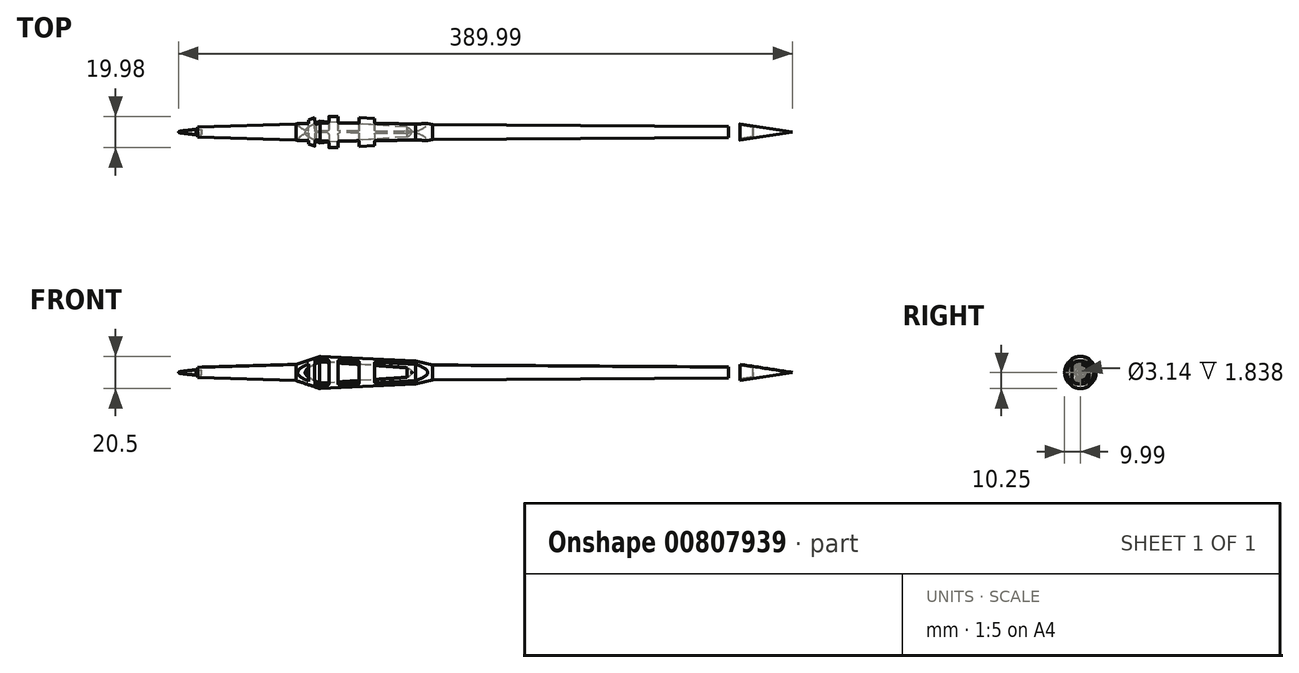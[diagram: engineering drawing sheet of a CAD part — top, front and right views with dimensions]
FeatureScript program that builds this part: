
annotation { "Feature Type Name" : "Feature", "Feature Type Description" : "" }
export const myFeature = defineFeature(function(context is Context, id is Id, definition is map)
    precondition{}
    {
        {
            var Q0;
            Q0=qCreatedBy(makeId("Right.planeOp"),FACE);
            var sketch = newSketch(context, id + "F0", { "sketchPlane" : qUnion([Q0])});
            skCircle(sketch, "E0", {"center": v(0, 0) * mm, "radius": 16.1 * mm});
            skSolve(sketch);
        }
        {
            var Q0;
            Q0=qCreatedBy(makeId("Front.planeOp"),FACE);
            var sketch = newSketch(context, id + "F1", { "sketchPlane" : qUnion([Q0])});
            skLineSegment(sketch, "E1", {"start": v(-173.44, 0) * mm, "end": v(-110.98, 0) * mm});
            skLineSegment(sketch, "E2", {"start": v(-110.98, 0) * mm, "end": v(-110.98, 5.13) * mm});
            skLineSegment(sketch, "E3", {"start": v(-110.98, 5.13) * mm, "end": v(-173.44, 3.3) * mm});
            skLineSegment(sketch, "E4", {"start": v(-173.44, 3.3) * mm, "end": v(-173.43, 2.8) * mm});
            skLineSegment(sketch, "E5", {"start": v(-173.43, 2.8) * mm, "end": v(-171.93, 0) * mm});
            skSolve(sketch);
        }
        {
            var Q0;
            Q0 = qSketchRegion(id + "F1", true);
            var Q1;
            Q1=sQuery(id+"F0.wireOp",EDGE,"E0");
            revolve(context, id + "F2", {"surfaceOperationType" : NewSurfaceOperationType.NEW, "entities" : qUnion([Q0]), "axis" : qUnion([Q1]), "revolveType" : RevolveType.FULL});
        }
        {
            var Q0;
            Q0=qCreatedBy(makeId("Front.planeOp"),FACE);
            var sketch = newSketch(context, id + "F3", { "sketchPlane" : qUnion([Q0])});
            skLineSegment(sketch, "E6.0", {"start": v(-110.98, -5.13) * mm, "end": v(-110.98, 5.13) * mm});
            skLineSegment(sketch, "E7", {"start": v(-110.98, 5.13) * mm, "end": v(-95.6, 10.25) * mm});
            skLineSegment(sketch, "E8", {"start": v(-95.6, 10.25) * mm, "end": v(-35.2, 7.33) * mm});
            skLineSegment(sketch, "E9", {"start": v(-35.2, 7.33) * mm, "end": v(-24.39, 4.74) * mm});
            skLineSegment(sketch, "E10", {"start": v(-24.39, 4.74) * mm, "end": v(-24.39, 0) * mm});
            skLineSegment(sketch, "E11", {"start": v(-24.39, 0) * mm, "end": v(-110.98, 0) * mm});
            skSolve(sketch);
        }
        {
            var Q0;
            Q0 = qSketchRegion(id + "F3", true);
            var Q1;
            Q1=makeQuery(id+"F2.opRevolve","SWEPT_EDGE",EDGE,{"disambiguationData":[OSD([sQuery(id+"F1.wireOp",EDGE,"E2"),sQuery(id+"F1.wireOp",EDGE,"E3")])]});
            revolve(context, id + "F4", {"surfaceOperationType" : NewSurfaceOperationType.NEW, "entities" : qUnion([Q0]), "axis" : qUnion([Q1]), "revolveType" : RevolveType.FULL});
        }
        {
            var Q0;
            Q0=qCreatedBy(makeId("Front.planeOp"),FACE);
            var sketch = newSketch(context, id + "F5", { "sketchPlane" : qUnion([Q0])});
            skLineSegment(sketch, "E12.0", {"start": v(-24.39, 4.74) * mm, "end": v(-24.39, -4.74) * mm});
            skLineSegment(sketch, "E13", {"start": v(-24.39, 4.74) * mm, "end": v(163.57, 3.5) * mm});
            skLineSegment(sketch, "E14", {"start": v(163.57, 3.5) * mm, "end": v(163.57, 0) * mm});
            skLineSegment(sketch, "E15", {"start": v(163.57, 0) * mm, "end": v(-24.39, 0) * mm});
            skSolve(sketch);
        }
        {
            var Q0;
            Q0 = qSketchRegion(id + "F5", true);
            var Q1;
            Q1=makeQuery(id+"F4.opRevolve","SWEPT_EDGE",EDGE,{"disambiguationData":[OSD([sQuery(id+"F3.wireOp",EDGE,"E9"),sQuery(id+"F3.wireOp",EDGE,"E10")])]});
            revolve(context, id + "F6", {"operationType" : NewBodyOperationType.ADD, "surfaceOperationType" : NewSurfaceOperationType.NEW, "entities" : qUnion([Q0]), "axis" : qUnion([Q1]), "revolveType" : RevolveType.FULL});
        }
        {
            var Q0;
            Q0=qCreatedBy(makeId("Front.planeOp"),FACE);
            var sketch = newSketch(context, id + "F7", { "sketchPlane" : qUnion([Q0])});
            skLineSegment(sketch, "E16", {"start": v(170.8, -5.14) * mm, "end": v(204.34, 0) * mm});
            skLineSegment(sketch, "E17", {"start": v(204.34, 0) * mm, "end": v(179.09, 0) * mm});
            skPoint(sketch, "E18.orphan", {"position": v(170.8, 5.14) * mm});
            skLineSegment(sketch, "E19", {"start": v(170.8, -5.14) * mm, "end": v(170.8, -4.26) * mm});
            skLineSegment(sketch, "E20", {"start": v(170.8, -4.26) * mm, "end": v(179.09, -3) * mm});
            skLineSegment(sketch, "E21", {"start": v(179.09, -3) * mm, "end": v(179.09, 0) * mm});
            skPoint(sketch, "E22.orphan", {"position": v(170.8, 0) * mm});
            skSolve(sketch);
        }
        {
            var Q0;
            Q0 = qSketchRegion(id + "F7", true);
            var Q1;
            Q1=sQuery(id+"F7.wireOp",EDGE,"E17");
            revolve(context, id + "F8", {"surfaceOperationType" : NewSurfaceOperationType.NEW, "entities" : qUnion([Q0]), "axis" : qUnion([Q1]), "revolveType" : RevolveType.FULL});
        }
        {
            var Q0;
            Q0=qCreatedBy(makeId("Front.planeOp"),FACE);
            var sketch = newSketch(context, id + "F9", { "sketchPlane" : qUnion([Q0])});
            skLineSegment(sketch, "E23", {"start": v(-105.41, 0) * mm, "end": v(-37.44, 0) * mm});
            skLineSegment(sketch, "E24", {"start": v(-96.12, 6.85) * mm, "end": v(-40.55, 3.12) * mm});
            skFitSpline(sketch, "E25", {"points": [v(-40.55, 3.12) * mm, v(-39.27, 2.42) * mm, v(-38.02, 1.33) * mm, v(-37.56, 0.61) * mm, v(-37.44, 0) * mm], "startDerivative": vector(4.44, -2.14) * mm, "endDerivative": vector(0.4, -3.29) * mm});
            skFitSpline(sketch, "E26", {"points": [v(-105.41, 0) * mm, v(-105.33, 0.62) * mm, v(-104.64, 1.81) * mm, v(-103.44, 2.78) * mm, v(-101.54, 3.98) * mm, v(-98.36, 5.7) * mm, v(-96.12, 6.85) * mm], "startDerivative": vector(0.12, 5.92) * mm, "endDerivative": vector(10.8, 5.6) * mm});
            skSolve(sketch);
        }
        {
            var Q0;
            Q0 = qSketchRegion(id + "F9", true);
            var Q1;
            Q1=sQuery(id+"F9.wireOp",EDGE,"E23");
            revolve(context, id + "F10", {"surfaceOperationType" : NewSurfaceOperationType.NEW, "entities" : qUnion([Q0]), "axis" : qUnion([Q1]), "revolveType" : RevolveType.FULL});
        }
        {
            var Q0;
            Q0=qCreatedBy(makeId("Front.planeOp"),FACE);
            cPlane(context, id + "F11", {"entities" : qUnion([Q0]), "cplaneType" : CPlaneType.OFFSET, "offset" : 5.5 * mm, "width" : 150 * mm, "height" : 150 * mm});
        }
        {
            var Q0;
            Q0=qCreatedBy(id+"F11.planeOp",FACE);
            var sketch = newSketch(context, id + "F12", { "sketchPlane" : qUnion([Q0])});
            skLineSegment(sketch, "E27", {"start": v(-103.15, 5.55) * mm, "end": v(-103.15, 0) * mm});
            skLineSegment(sketch, "E28", {"start": v(-103.15, 0) * mm, "end": v(-109.96, 0) * mm});
            skFitSpline(sketch, "E29", {"points": [v(-109.96, 0) * mm, v(-109.82, 0.74) * mm, v(-109.26, 1.7) * mm, v(-107.77, 3.02) * mm, v(-103.15, 5.55) * mm], "startDerivative": vector(0.52, 4.74) * mm, "endDerivative": vector(12.88, 6.48) * mm});
            skPoint(sketch, "E30.orphan", {"position": v(-72.07, 0) * mm});
            skLineSegment(sketch, "E31", {"start": v(-99.33, 0) * mm, "end": v(-90.18, 0) * mm});
            skLineSegment(sketch, "E32", {"start": v(-99.33, 0) * mm, "end": v(-99.05, 6.84) * mm});
            skLineSegment(sketch, "E33", {"start": v(-98.28, 7.82) * mm, "end": v(-96.53, 8.42) * mm});
            skLineSegment(sketch, "E34", {"start": v(-90.18, 0) * mm, "end": v(-90.18, 7.22) * mm});
            skLineSegment(sketch, "E35", {"start": v(-84.46, 0) * mm, "end": v(-84.46, 6.81) * mm});
            skLineSegment(sketch, "E36", {"start": v(-96.15, 8.48) * mm, "end": v(-91.13, 8.22) * mm});
            skLineSegment(sketch, "E37", {"start": v(-70.96, 0) * mm, "end": v(-70.96, 6.78) * mm});
            skLineSegment(sketch, "E38", {"start": v(-61.15, 0) * mm, "end": v(-61.15, 5.96) * mm});
            skFitSpline(sketch, "E39", {"points": [v(-35.21, 5.3) * mm, v(-33, 4.43) * mm, v(-30.49, 3.26) * mm, v(-28.4, 1.84) * mm, v(-27.66, 0.93) * mm, v(-27.4, 0) * mm], "startDerivative": vector(9.73, -3.74) * mm, "endDerivative": vector(1.3, -6.7) * mm});
            skArc(sketch, "E40", {"start": v(-60.47, 6.62) * mm, "mid": v(-60.95, 6.44) * mm, "end": v(-61.15, 5.96) * mm});
            skArc(sketch, "E41", {"start": v(-70.96, 6.78) * mm, "mid": v(-71.05, 7.04) * mm, "end": v(-71.28, 7.18) * mm});
            skArc(sketch, "E42.filletArc", {"start": v(-83.4, 7.81) * mm, "mid": v(-84.15, 7.54) * mm, "end": v(-84.46, 6.81) * mm});
            skArc(sketch, "E43.filletArc", {"start": v(-90.18, 7.22) * mm, "mid": v(-90.45, 7.9) * mm, "end": v(-91.13, 8.22) * mm});
            skFitSpline(sketch, "E44", {"points": [v(-99.05, 6.84) * mm, v(-98.95, 7.26) * mm, v(-98.7, 7.57) * mm, v(-98.28, 7.82) * mm], "startDerivative": vector(0.2, 1.33) * mm, "endDerivative": vector(1.27, 0.66) * mm});
            skLineSegment(sketch, "E45", {"start": v(-83.4, 7.81) * mm, "end": v(-71.28, 7.18) * mm});
            skLineSegment(sketch, "E46", {"start": v(-60.47, 6.62) * mm, "end": v(-35.21, 5.3) * mm});
            skLineSegment(sketch, "E47.trimOffspring", {"start": v(-61.15, 0) * mm, "end": v(-27.4, 0) * mm});
            skLineSegment(sketch, "E48.trimOffspring", {"start": v(-84.46, 0) * mm, "end": v(-70.96, 0) * mm});
            skPoint(sketch, "E49.visualSharp", {"position": v(-96.34, 8.49) * mm});
            skArc(sketch, "E49.filletArc", {"start": v(-96.15, 8.48) * mm, "mid": v(-96.34, 8.47) * mm, "end": v(-96.53, 8.42) * mm});
            skSolve(sketch);
        }
        {
            var Q0;
            Q0 = qSketchRegion(id + "F12", true);
            var Q1;
            Q1=sQuery(id+"F12.wireOp",EDGE,"E28");
            revolve(context, id + "F13", {"surfaceOperationType" : NewSurfaceOperationType.NEW, "entities" : qUnion([Q0]), "axis" : qUnion([Q1]), "revolveType" : RevolveType.FULL});
        }
        {
            var Q0;
            Q0=makeQuery(id+"F13.opRevolve","SWEPT_BODY",BODY,{"disambiguationData":[OSD([sQuery(id+"F12.wireOp",EDGE,"E27"),sQuery(id+"F12.wireOp",EDGE,"E28"),sQuery(id+"F12.wireOp",EDGE,"E29")])]});
            var Q1;
            Q1=makeQuery(id+"F13.opRevolve","SWEPT_BODY",BODY,{"disambiguationData":[OSD([sQuery(id+"F12.wireOp",EDGE,"E31"),sQuery(id+"F12.wireOp",EDGE,"E32"),sQuery(id+"F12.wireOp",EDGE,"E33"),sQuery(id+"F12.wireOp",EDGE,"E34"),sQuery(id+"F12.wireOp",EDGE,"E36"),sQuery(id+"F12.wireOp",EDGE,"E43.filletArc"),sQuery(id+"F12.wireOp",EDGE,"E44")])]});
            var Q2;
            Q2=makeQuery(id+"F13.opRevolve","SWEPT_BODY",BODY,{"disambiguationData":[OSD([sQuery(id+"F12.wireOp",EDGE,"E35"),sQuery(id+"F12.wireOp",EDGE,"E37"),sQuery(id+"F12.wireOp",EDGE,"E41"),sQuery(id+"F12.wireOp",EDGE,"E42.filletArc"),sQuery(id+"F12.wireOp",EDGE,"E45"),sQuery(id+"F12.wireOp",EDGE,"E48.trimOffspring")])]});
            var Q3;
            Q3=makeQuery(id+"F13.opRevolve","SWEPT_BODY",BODY,{"disambiguationData":[OSD([sQuery(id+"F12.wireOp",EDGE,"E38"),sQuery(id+"F12.wireOp",EDGE,"E39"),sQuery(id+"F12.wireOp",EDGE,"E40"),sQuery(id+"F12.wireOp",EDGE,"E46"),sQuery(id+"F12.wireOp",EDGE,"E47.trimOffspring")])]});
            var Q4;
            Q4=qCreatedBy(makeId("Front.planeOp"),FACE);
            mirror(context, id + "F14", {"entities" : qUnion([Q0, Q1, Q2, Q3]), "mirrorPlane" : qUnion([Q4])});
        }
        {
            var Q0;
            Q0=makeQuery(id+"F14.opPattern","COPY",BODY,{"derivedFrom":makeQuery(id+"F13.opRevolve","SWEPT_BODY",BODY,{"disambiguationData":[OSD([sQuery(id+"F12.wireOp",EDGE,"E27"),sQuery(id+"F12.wireOp",EDGE,"E28"),sQuery(id+"F12.wireOp",EDGE,"E29")])]}),"instanceName":"1"});
            var Q1;
            Q1=makeQuery(id+"F13.opRevolve","SWEPT_BODY",BODY,{"disambiguationData":[OSD([sQuery(id+"F12.wireOp",EDGE,"E27"),sQuery(id+"F12.wireOp",EDGE,"E28"),sQuery(id+"F12.wireOp",EDGE,"E29")])]});
            var Q2;
            Q2=makeQuery(id+"F13.opRevolve","SWEPT_BODY",BODY,{"disambiguationData":[OSD([sQuery(id+"F12.wireOp",EDGE,"E31"),sQuery(id+"F12.wireOp",EDGE,"E32"),sQuery(id+"F12.wireOp",EDGE,"E33"),sQuery(id+"F12.wireOp",EDGE,"E34"),sQuery(id+"F12.wireOp",EDGE,"E36"),sQuery(id+"F12.wireOp",EDGE,"E43.filletArc"),sQuery(id+"F12.wireOp",EDGE,"E44")])]});
            var Q3;
            Q3=makeQuery(id+"F13.opRevolve","SWEPT_BODY",BODY,{"disambiguationData":[OSD([sQuery(id+"F12.wireOp",EDGE,"E35"),sQuery(id+"F12.wireOp",EDGE,"E37"),sQuery(id+"F12.wireOp",EDGE,"E41"),sQuery(id+"F12.wireOp",EDGE,"E42.filletArc"),sQuery(id+"F12.wireOp",EDGE,"E45"),sQuery(id+"F12.wireOp",EDGE,"E48.trimOffspring")])]});
            var Q4;
            Q4=makeQuery(id+"F13.opRevolve","SWEPT_BODY",BODY,{"disambiguationData":[OSD([sQuery(id+"F12.wireOp",EDGE,"E38"),sQuery(id+"F12.wireOp",EDGE,"E39"),sQuery(id+"F12.wireOp",EDGE,"E40"),sQuery(id+"F12.wireOp",EDGE,"E46"),sQuery(id+"F12.wireOp",EDGE,"E47.trimOffspring")])]});
            var Q5;
            Q5=makeQuery(id+"F14.opPattern","COPY",BODY,{"derivedFrom":makeQuery(id+"F13.opRevolve","SWEPT_BODY",BODY,{"disambiguationData":[OSD([sQuery(id+"F12.wireOp",EDGE,"E38"),sQuery(id+"F12.wireOp",EDGE,"E39"),sQuery(id+"F12.wireOp",EDGE,"E40"),sQuery(id+"F12.wireOp",EDGE,"E46"),sQuery(id+"F12.wireOp",EDGE,"E47.trimOffspring")])]}),"instanceName":"1"});
            var Q6;
            Q6=makeQuery(id+"F14.opPattern","COPY",BODY,{"derivedFrom":makeQuery(id+"F13.opRevolve","SWEPT_BODY",BODY,{"disambiguationData":[OSD([sQuery(id+"F12.wireOp",EDGE,"E35"),sQuery(id+"F12.wireOp",EDGE,"E37"),sQuery(id+"F12.wireOp",EDGE,"E41"),sQuery(id+"F12.wireOp",EDGE,"E42.filletArc"),sQuery(id+"F12.wireOp",EDGE,"E45"),sQuery(id+"F12.wireOp",EDGE,"E48.trimOffspring")])]}),"instanceName":"1"});
            var Q7;
            Q7=makeQuery(id+"F14.opPattern","COPY",BODY,{"derivedFrom":makeQuery(id+"F13.opRevolve","SWEPT_BODY",BODY,{"disambiguationData":[OSD([sQuery(id+"F12.wireOp",EDGE,"E31"),sQuery(id+"F12.wireOp",EDGE,"E32"),sQuery(id+"F12.wireOp",EDGE,"E33"),sQuery(id+"F12.wireOp",EDGE,"E34"),sQuery(id+"F12.wireOp",EDGE,"E36"),sQuery(id+"F12.wireOp",EDGE,"E43.filletArc"),sQuery(id+"F12.wireOp",EDGE,"E44")])]}),"instanceName":"1"});
            var Q8;
            Q8=makeQuery(id+"F4.opRevolve","SWEPT_BODY",BODY,{"disambiguationData":[OSD([sQuery(id+"F3.wireOp",EDGE,"E6.0"),sQuery(id+"F3.wireOp",EDGE,"E7"),sQuery(id+"F3.wireOp",EDGE,"E8"),sQuery(id+"F3.wireOp",EDGE,"E9"),sQuery(id+"F3.wireOp",EDGE,"E10"),sQuery(id+"F3.wireOp",EDGE,"E11")])]});
            booleanBodies(context, id + "F15", {"operationType" : BooleanOperationType.SUBTRACTION, "tools" : qUnion([Q0, Q1, Q2, Q3, Q4, Q5, Q6, Q7]), "targets" : qUnion([Q8])});
        }
        {
            var Q0;
            Q0=qCreatedBy(makeId("Front.planeOp"),FACE);
            var sketch = newSketch(context, id + "F16", { "sketchPlane" : qUnion([Q0])});
            skLineSegment(sketch, "E50", {"start": v(0, 0) * mm, "end": v(-193.66, 0) * mm});
            skFitSpline(sketch, "E51", {"points": [v(-185.65, 0) * mm, v(-185.54, 0.27) * mm, v(-184.9, 0.47) * mm, v(-176.75, 1.45) * mm, v(-174.46, 1.57) * mm], "startDerivative": vector(0.87, 3.18) * mm, "endDerivative": vector(6.26, 0.09) * mm});
            skLineSegment(sketch, "E52", {"start": v(-174.46, 1.57) * mm, "end": v(-170.93, 1.57) * mm});
            skLineSegment(sketch, "E53", {"start": v(-170.93, 1.57) * mm, "end": v(-170.93, 0) * mm});
            skSolve(sketch);
        }
        {
            var Q0;
            Q0 = qSketchRegion(id + "F16", true);
            var Q1;
            Q1=sQuery(id+"F16.wireOp",EDGE,"E50");
            revolve(context, id + "F17", {"surfaceOperationType" : NewSurfaceOperationType.NEW, "entities" : qUnion([Q0]), "axis" : qUnion([Q1]), "revolveType" : RevolveType.FULL});
        }
        {
            var Q0;
            Q0=makeQuery(id+"F17.opRevolve","SWEPT_BODY",BODY,{"disambiguationData":[OSD([sQuery(id+"F16.wireOp",EDGE,"E50"),sQuery(id+"F16.wireOp",EDGE,"E51"),sQuery(id+"F16.wireOp",EDGE,"E52"),sQuery(id+"F16.wireOp",EDGE,"E53")])]});
            transform(context, id + "F18", {"entities" : qUnion([Q0]), "transformType" : TransformType.TRANSLATION_3D, "dx" : 0 * mm, "dy" : 0 * mm, "dz" : 0 * mm, "makeCopy" : true});
        }
        {
            var Q0;
            Q0=makeQuery(id+"F18.opPattern","COPY",BODY,{"derivedFrom":makeQuery(id+"F17.opRevolve","SWEPT_BODY",BODY,{"disambiguationData":[OSD([sQuery(id+"F16.wireOp",EDGE,"E50"),sQuery(id+"F16.wireOp",EDGE,"E51"),sQuery(id+"F16.wireOp",EDGE,"E52"),sQuery(id+"F16.wireOp",EDGE,"E53")])]}),"instanceName":"1"});
            var Q1;
            Q1=makeQuery(id+"F2.opRevolve","SWEPT_BODY",BODY,{"disambiguationData":[OSD([sQuery(id+"F1.wireOp",EDGE,"E1"),sQuery(id+"F1.wireOp",EDGE,"E2"),sQuery(id+"F1.wireOp",EDGE,"E3"),sQuery(id+"F1.wireOp",EDGE,"EPHL8iwW-0kiM-ldp9-sbAc-f7dRZdCR8gQH")])]});
            booleanBodies(context, id + "F19", {"operationType" : BooleanOperationType.SUBTRACTION, "tools" : qUnion([Q0]), "targets" : qUnion([Q1])});
        }
        {
            var Q0;
            Q0=makeQuery(id+"F10.opRevolve","SWEPT_BODY",BODY,{"disambiguationData":[OSD([sQuery(id+"F9.wireOp",EDGE,"E23"),sQuery(id+"F9.wireOp",EDGE,"E24"),sQuery(id+"F9.wireOp",EDGE,"E25"),sQuery(id+"F9.wireOp",EDGE,"E26")])]});
            transform(context, id + "F20", {"entities" : qUnion([Q0]), "transformType" : TransformType.TRANSLATION_3D, "dx" : 0 * mm, "dy" : 0 * mm, "dz" : 0 * mm, "makeCopy" : true});
        }
        {
            var Q0;
            Q0=makeQuery(id+"F20.opPattern","COPY",BODY,{"derivedFrom":makeQuery(id+"F10.opRevolve","SWEPT_BODY",BODY,{"disambiguationData":[OSD([sQuery(id+"F9.wireOp",EDGE,"E23"),sQuery(id+"F9.wireOp",EDGE,"E24"),sQuery(id+"F9.wireOp",EDGE,"E25"),sQuery(id+"F9.wireOp",EDGE,"E26")])]}),"instanceName":"1"});
            var Q1;
            Q1=makeQuery(id+"F4.opRevolve","SWEPT_BODY",BODY,{"disambiguationData":[OSD([sQuery(id+"F3.wireOp",EDGE,"E6.0"),sQuery(id+"F3.wireOp",EDGE,"E7"),sQuery(id+"F3.wireOp",EDGE,"E8"),sQuery(id+"F3.wireOp",EDGE,"E9"),sQuery(id+"F3.wireOp",EDGE,"E10"),sQuery(id+"F3.wireOp",EDGE,"E11")])]});
            booleanBodies(context, id + "F21", {"operationType" : BooleanOperationType.SUBTRACTION, "tools" : qUnion([Q0]), "targets" : qUnion([Q1])});
        }
    });
